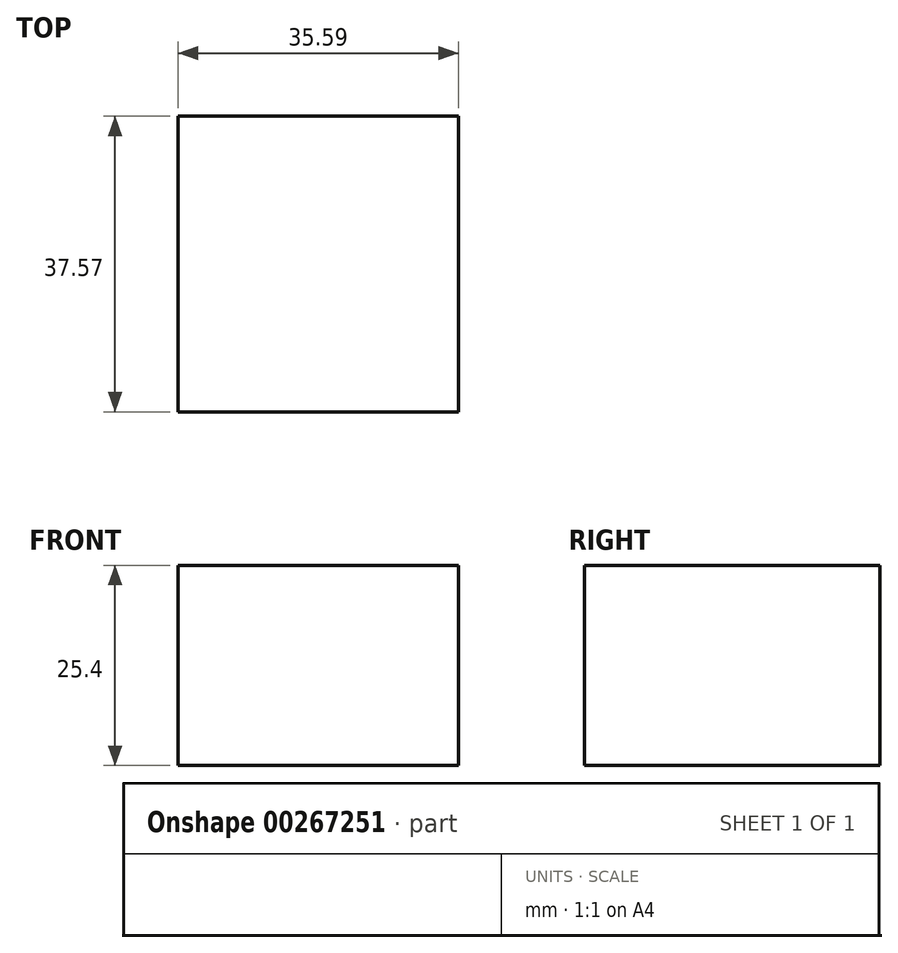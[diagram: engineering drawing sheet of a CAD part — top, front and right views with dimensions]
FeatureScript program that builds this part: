
annotation { "Feature Type Name" : "Feature", "Feature Type Description" : "" }
export const myFeature = defineFeature(function(context is Context, id is Id, definition is map)
    precondition{}
    {
        {
            var Q0;
            Q0=qCreatedBy(makeId("Top.planeOp"),FACE);
            var sketch = newSketch(context, id + "F0", { "sketchPlane" : qUnion([Q0])});
            skLineSegment(sketch, "E0.bottom", {"start": v(0, 0) * mm, "end": v(-35.6, 0) * mm});
            skLineSegment(sketch, "E0.top", {"start": v(0, -37.57) * mm, "end": v(-35.6, -37.57) * mm});
            skLineSegment(sketch, "E0.left", {"start": v(0, 0) * mm, "end": v(0, -37.57) * mm});
            skLineSegment(sketch, "E0.right", {"start": v(-35.6, 0) * mm, "end": v(-35.6, -37.57) * mm});
            skSolve(sketch);
        }
        {
            var Q0;
            Q0=makeQuery(id+"F0.imprint","IMPRINT",FACE,{"disambiguationData":[TD([[makeQuery(id+"F0.imprint","IMPRINT",EDGE,{"derivedFrom":sQuery(id+"F0.wireOp",EDGE,"E0.bottom")}),1.0]])]});
            extrude(context, id + "F1", {"entities" : qUnion([Q0]), "depth" : 25.4 * mm});
        }
    });
